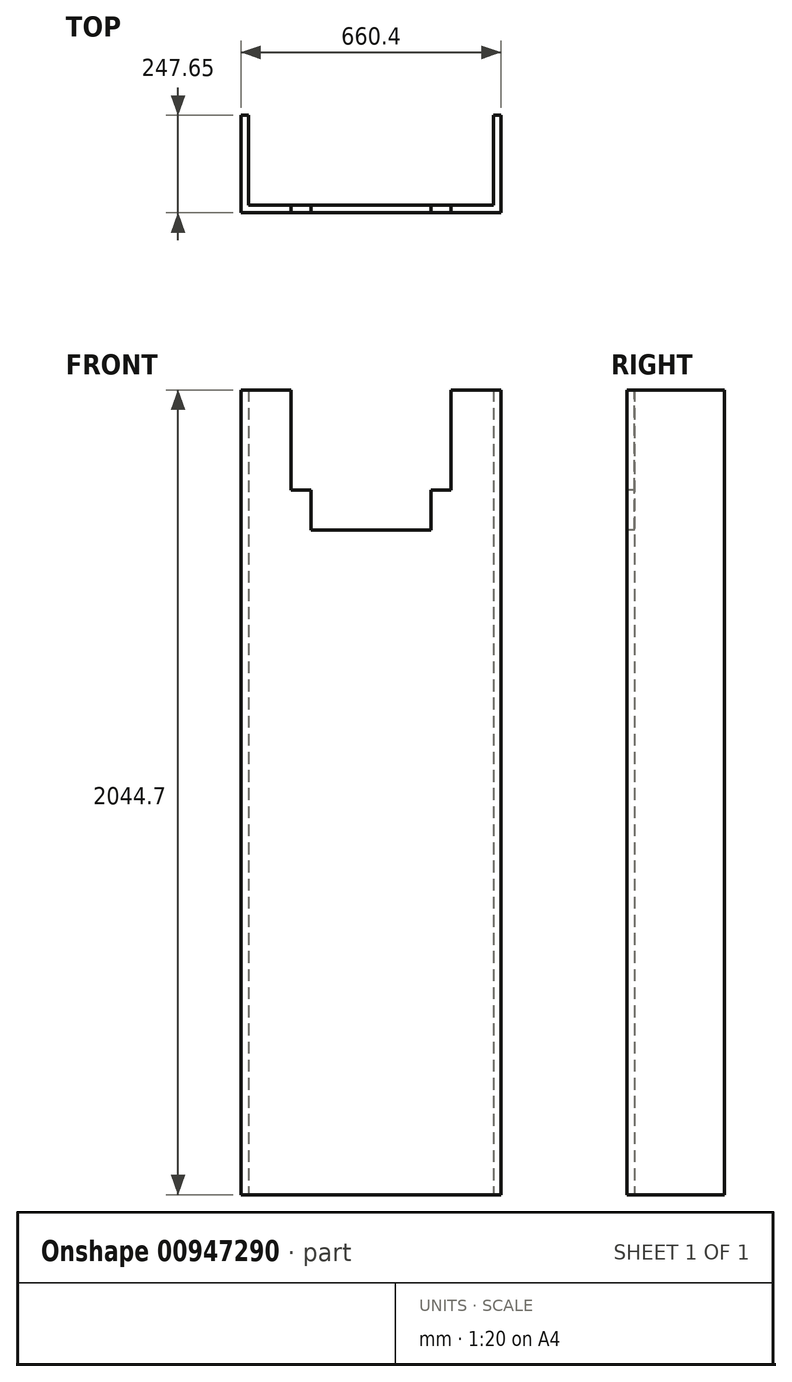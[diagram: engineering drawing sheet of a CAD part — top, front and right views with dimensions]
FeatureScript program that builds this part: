
annotation { "Feature Type Name" : "Feature", "Feature Type Description" : "" }
export const myFeature = defineFeature(function(context is Context, id is Id, definition is map)
    precondition{}
    {
        {
            var Q0;
            Q0=qCreatedBy(makeId("Top.planeOp"),FACE);
            var sketch = newSketch(context, id + "F0", { "sketchPlane" : qUnion([Q0])});
            skLineSegment(sketch, "E0", {"start": v(311.15, 19.05) * mm, "end": v(311.15, 247.65) * mm});
            skLineSegment(sketch, "E1", {"start": v(311.15, 247.65) * mm, "end": v(330.2, 247.65) * mm});
            skLineSegment(sketch, "E2", {"start": v(330.2, 247.65) * mm, "end": v(330.2, 0) * mm});
            skLineSegment(sketch, "E3", {"start": v(330.2, 0) * mm, "end": v(-330.2, 0) * mm});
            skLineSegment(sketch, "E4", {"start": v(-330.2, 0) * mm, "end": v(-330.2, 247.65) * mm});
            skLineSegment(sketch, "E5", {"start": v(-330.2, 247.65) * mm, "end": v(-311.15, 247.65) * mm});
            skLineSegment(sketch, "E6", {"start": v(-311.15, 247.65) * mm, "end": v(-311.15, 19.05) * mm});
            skLineSegment(sketch, "E7", {"start": v(-311.15, 19.05) * mm, "end": v(311.15, 19.05) * mm});
            skSolve(sketch);
        }
        {
            var Q0;
            Q0 = qSketchRegion(id + "F0", true);
            extrude(context, id + "F1", {"entities" : qUnion([Q0]), "endBound" : BoundingType.SYMMETRIC, "depth" : 2044.7 * mm, "offsetDistance" : 25.4 * mm});
        }
        {
            var Q0;
            Q0=makeQuery(id+"F1.opExtrude","SWEPT_FACE",FACE,{"disambiguationData":[OSD([sQuery(id+"F0.wireOp",EDGE,"E3")])]});
            var sketch = newSketch(context, id + "F2", { "sketchPlane" : qUnion([Q0])});
            skLineSegment(sketch, "E8", {"start": v(-203.2, 1022.35) * mm, "end": v(-203.2, 768.35) * mm});
            skLineSegment(sketch, "E9", {"start": v(-203.2, 768.35) * mm, "end": v(-152.4, 768.35) * mm});
            skLineSegment(sketch, "E10", {"start": v(-152.4, 768.35) * mm, "end": v(-152.4, 666.75) * mm});
            skLineSegment(sketch, "E11", {"start": v(-152.4, 666.75) * mm, "end": v(152.4, 666.75) * mm});
            skLineSegment(sketch, "E12", {"start": v(152.4, 666.75) * mm, "end": v(152.4, 768.35) * mm});
            skLineSegment(sketch, "E13", {"start": v(152.4, 768.35) * mm, "end": v(203.2, 768.35) * mm});
            skLineSegment(sketch, "E14", {"start": v(203.2, 768.35) * mm, "end": v(203.2, 1022.35) * mm});
            skLineSegment(sketch, "E15", {"start": v(203.2, 1022.35) * mm, "end": v(-203.2, 1022.35) * mm});
            skSolve(sketch);
        }
        {
            var Q0;
            Q0=makeQuery(id+"F2.imprint","IMPRINT",FACE,{"disambiguationData":[TD([[makeQuery(id+"F2.imprint","IMPRINT",EDGE,{"derivedFrom":sQuery(id+"F2.wireOp",EDGE,"E8")}),1.0]])]});
            extrude(context, id + "F3", {"entities" : qUnion([Q0]), "operationType" : NewBodyOperationType.REMOVE, "oppositeDirection" : true, "depth" : 25.4 * mm, "offsetDistance" : 25.4 * mm});
        }
        {
            var Q0;
            Q0=makeQuery(id+"F1.opExtrude","SWEPT_FACE",FACE,{"disambiguationData":[OSD([sQuery(id+"F0.wireOp",EDGE,"E3")])]});
            cPlane(context, id + "F4", {"entities" : qUnion([Q0]), "cplaneType" : CPlaneType.OFFSET, "offset" : 19.05 * mm, "oppositeDirection" : true, "width" : 152.4 * mm, "height" : 152.4 * mm});
        }
    });
